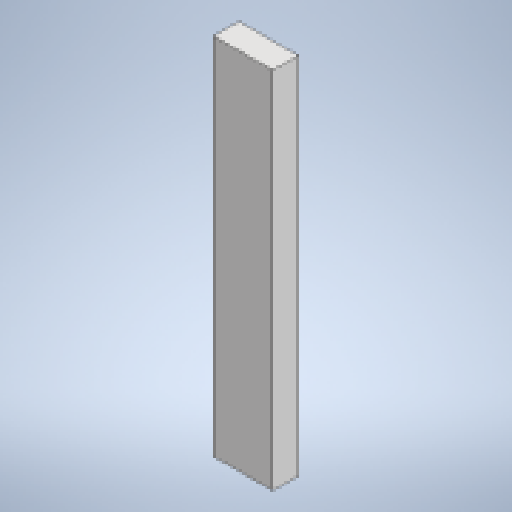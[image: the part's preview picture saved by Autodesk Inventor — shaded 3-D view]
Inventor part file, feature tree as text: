
AUTODESK INVENTOR PART (.ipt)
format: ipt  version: 2025.1 (Build 291241020, 241B)  size: 133,120 bytes
history: native  units: in
note: dims shown in document units (in); Inventor stores cm internally (conversion verified against a paired STEP export)
features: other x4, reference x3, extrude x1, sketch x1
ambient origin geometry x8: Origin, YZ Plane, XZ Plane, XY Plane, X Axis, Y Axis, Z Axis, Center Point
bodies: Solid1 (feature_tree)
feature tree (9):
  extrude  "Extrusion1"  Depth=3.5in
  sketch  "Sketch1"  dims[d1=1.5in d2=0.0in d3=3.5in]
  reference  "Reference1"
  reference  "Reference2"
  reference  "Reference3"
  other  "<userpath>\Documents\Tburn24\F_Legs2\F_Legs2.iam"
  other  "F_Legs2.iam"
  other  "side-side1:1"
  other  "side-side:2"
